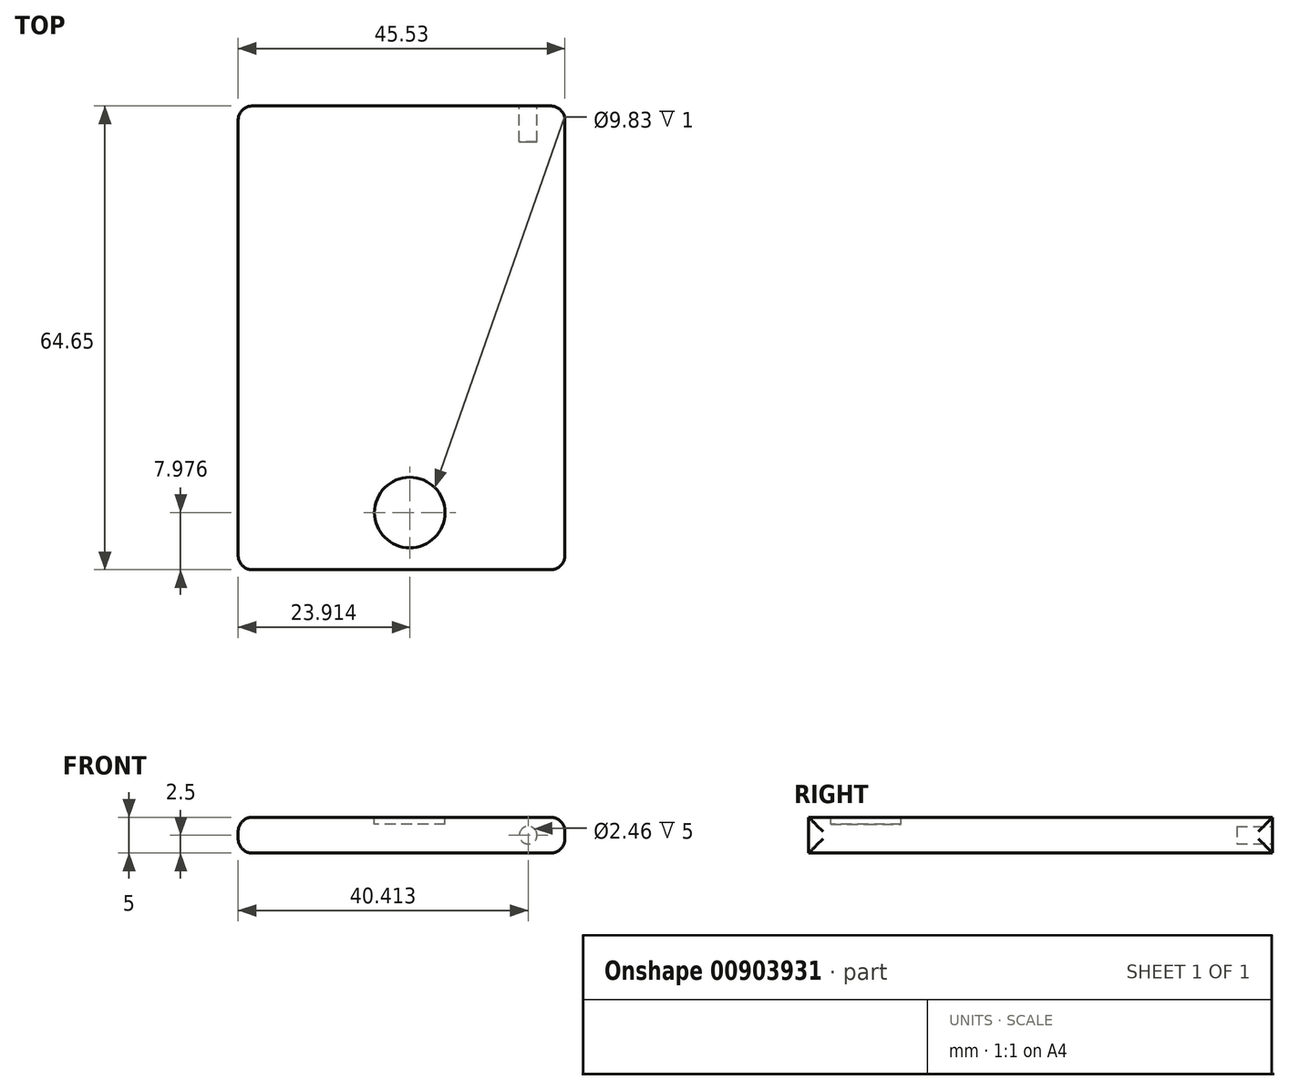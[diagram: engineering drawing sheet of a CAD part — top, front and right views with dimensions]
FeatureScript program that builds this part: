
annotation { "Feature Type Name" : "Feature", "Feature Type Description" : "" }
export const myFeature = defineFeature(function(context is Context, id is Id, definition is map)
    precondition{}
    {
        {
            var Q0;
            Q0=qCreatedBy(makeId("Top.planeOp"),FACE);
            var sketch = newSketch(context, id + "F0", { "sketchPlane" : qUnion([Q0])});
            skLineSegment(sketch, "E0.bottom", {"start": v(0, 0) * mm, "end": v(45.53, 0) * mm});
            skLineSegment(sketch, "E0.top", {"start": v(0, 64.65) * mm, "end": v(45.53, 64.65) * mm});
            skLineSegment(sketch, "E0.left", {"start": v(0, 0) * mm, "end": v(0, 64.65) * mm});
            skLineSegment(sketch, "E0.right", {"start": v(45.53, 0) * mm, "end": v(45.53, 64.65) * mm});
            skSolve(sketch);
        }
        {
            var Q0;
            Q0 = qSketchRegion(id + "F0", true);
            extrude(context, id + "F1", {"entities" : qUnion([Q0]), "depth" : 5 * mm, "offsetDistance" : 25 * mm});
        }
        {
            var Q0;
            Q0=makeQuery(id+"F1.opExtrude","SWEPT_FACE",FACE,{"disambiguationData":[OSD([sQuery(id+"F0.wireOp",EDGE,"E0.left")])]});
            var Q1;
            Q1=makeQuery(id+"F1.opExtrude","SWEPT_FACE",FACE,{"disambiguationData":[OSD([sQuery(id+"F0.wireOp",EDGE,"E0.right")])]});
            fillet(context, id + "F2", {"entities" : qUnion([Q0, Q1]), "radius" : 2 * mm, "tangentPropagation" : true, "allowEdgeOverflow" : false});
        }
        {
            var Q0;
            Q0=makeQuery(id+"F1.opExtrude","CAP_FACE",FACE,{"disambiguationData":[OSD([sQuery(id+"F0.wireOp",EDGE,"E0.bottom"),sQuery(id+"F0.wireOp",EDGE,"E0.top"),sQuery(id+"F0.wireOp",EDGE,"E0.left"),sQuery(id+"F0.wireOp",EDGE,"E0.right")])],"isStart":false});
            var sketch = newSketch(context, id + "F3", { "sketchPlane" : qUnion([Q0])});
            skCircle(sketch, "E1", {"center": v(23.91, 7.98) * mm, "radius": 4.91 * mm});
            skSolve(sketch);
        }
        {
            var Q0;
            Q0 = qSketchRegion(id + "F3", true);
            extrude(context, id + "F4", {"entities" : qUnion([Q0]), "operationType" : NewBodyOperationType.REMOVE, "oppositeDirection" : true, "depth" : 1 * mm, "offsetDistance" : 25 * mm});
        }
        {
            var Q0;
            Q0=makeQuery(id+"F1.opExtrude","SWEPT_FACE",FACE,{"disambiguationData":[OSD([sQuery(id+"F0.wireOp",EDGE,"E0.top")])]});
            var sketch = newSketch(context, id + "F5", { "sketchPlane" : qUnion([Q0])});
            skCircle(sketch, "E2", {"center": v(-40.41, 2.5) * mm, "radius": 1.23 * mm});
            skPoint(sketch, "E2.centerSnap0", {"position": v(-43.53, 2.5) * mm});
            skSolve(sketch);
        }
        {
            var Q0;
            Q0 = qSketchRegion(id + "F5", true);
            extrude(context, id + "F6", {"entities" : qUnion([Q0]), "operationType" : NewBodyOperationType.REMOVE, "oppositeDirection" : true, "depth" : 5 * mm, "offsetDistance" : 25 * mm});
        }
    });
